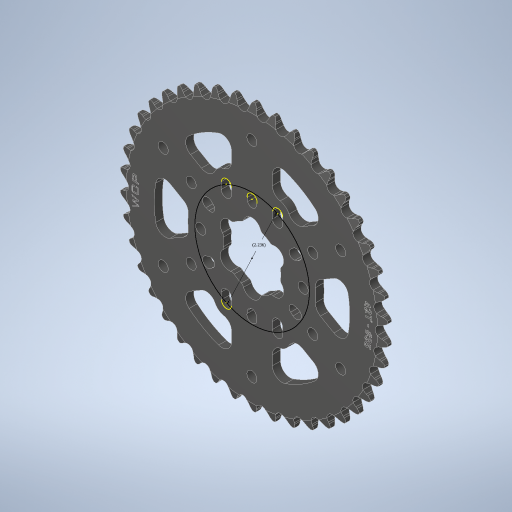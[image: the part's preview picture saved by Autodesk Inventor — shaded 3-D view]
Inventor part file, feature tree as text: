
AUTODESK INVENTOR PART (.ipt)
format: ipt  version: 2023.3 (Build 273359000, 359)  size: 1,779,712 bytes
history: native  units: in
note: dims shown in document units (in); Inventor stores cm internally (conversion verified against a paired STEP export)
features: sketch x1, other x1
ambient origin geometry x8: Origin, YZ Plane, XZ Plane, XY Plane, X Axis, Y Axis, Z Axis, Center Point
bodies: Solid1 (feature_tree)
feature tree (2):
  sketch  "Sketch4"  dims[d5=2.2361in]
  other  "Cut-Extrude4"
